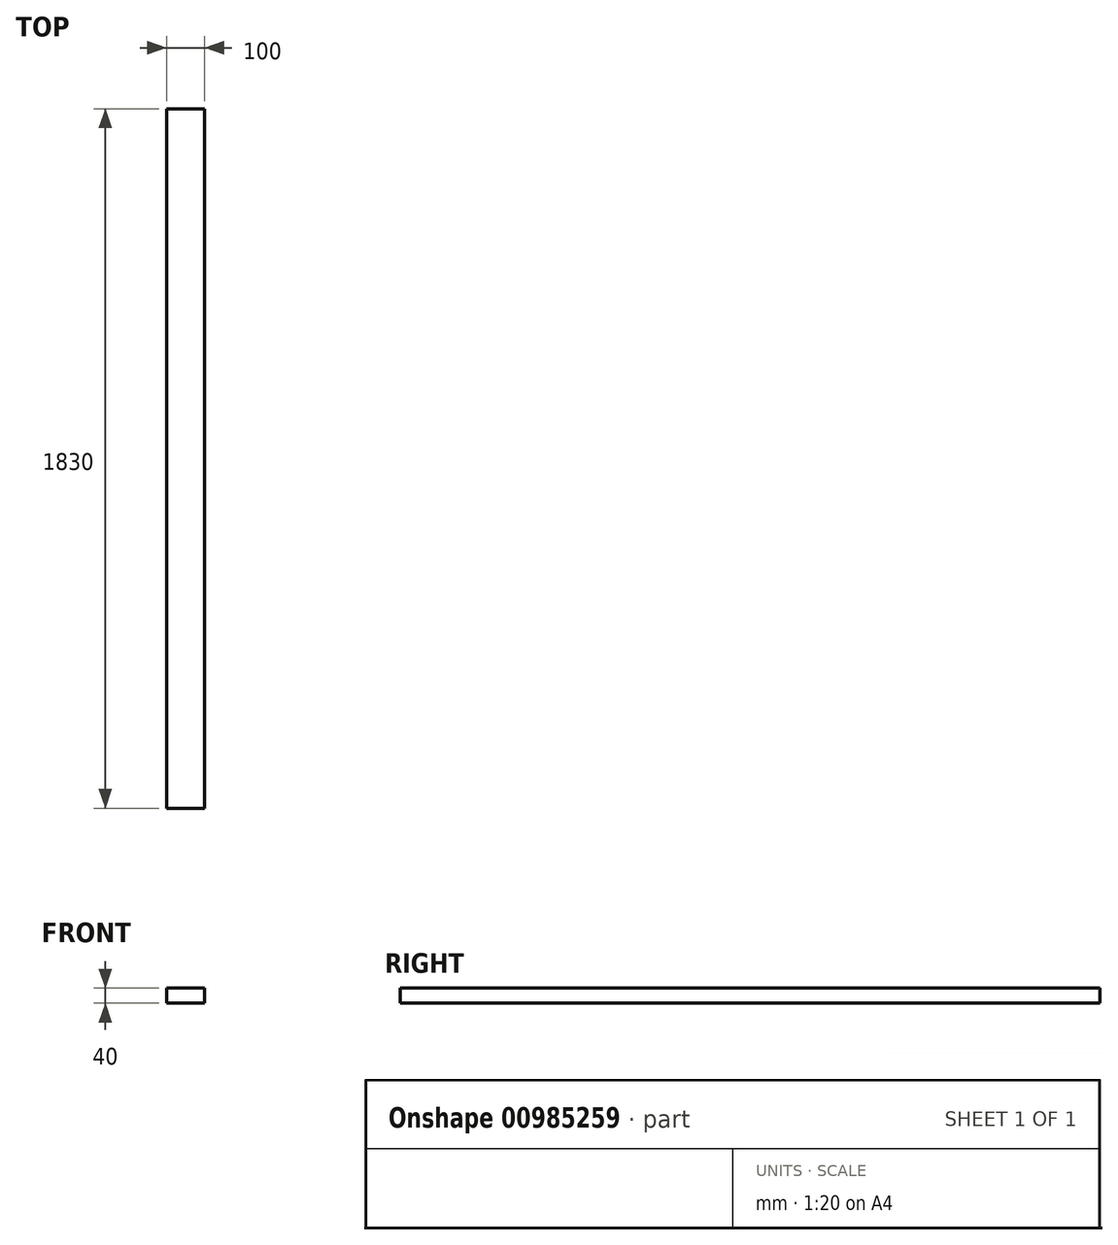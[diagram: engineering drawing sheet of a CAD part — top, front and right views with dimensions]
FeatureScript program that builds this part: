
annotation { "Feature Type Name" : "Feature", "Feature Type Description" : "" }
export const myFeature = defineFeature(function(context is Context, id is Id, definition is map)
    precondition{}
    {
        {
            var Q0;
            Q0=qCreatedBy(makeId("Front.planeOp"),FACE);
            var sketch = newSketch(context, id + "F0", { "sketchPlane" : qUnion([Q0])});
            skLineSegment(sketch, "E0.bottom", {"start": v(0, 0) * mm, "end": v(100, 0) * mm});
            skLineSegment(sketch, "E0.top", {"start": v(0, 40) * mm, "end": v(100, 40) * mm});
            skLineSegment(sketch, "E0.left", {"start": v(0, 0) * mm, "end": v(0, 40) * mm});
            skLineSegment(sketch, "E0.right", {"start": v(100, 0) * mm, "end": v(100, 40) * mm});
            skSolve(sketch);
        }
        {
            var Q0;
            Q0 = qSketchRegion(id + "F0", true);
            extrude(context, id + "F1", {"entities" : qUnion([Q0]), "depth" : 1830 * mm, "offsetDistance" : 25 * mm});
        }
    });
